# Revit family: FP_Revit_18_CID834RDTB4_Cooktop_90001222A
name_source: partatom
category: Specialty Equipment
revit_build: Autodesk Revit 2018 (Build: 20170223_1515(x64)
units: mm (PartAtom-declared; Revit-internal decimal feet)

## family parameters
Always vertical = Yes
Cut with Voids When Loaded = Yes
OmniClass Number = 23.40.40.14.17.11
OmniClass Title = Cookers, Ovens, Stoves
Part Type = Normal
Room Calculation Point = No
Round Connector Dimension = Use Diameter
Shared = No
Work Plane-Based = No

## types (3) — shared parameters
Cavity - Depth = 492 mm
Cavity - Width = 807 mm
Chassis - Depth = 490 mm
Chassis - Height = 52 mm
Chassis - Width = 800 mm
Clearance - Below Cooktop = 415 mm
Clearance - Overhead Non-Combustible = 500 mm  [stored 1.64042 ft]
Clearance - Rear = 50 mm  [stored 0.164042 ft]
Clearance - Side Combustible = 40 mm
Connector Description - Electrical = 220 - 240 V, or 380 - 415 V 2N or 380 - 415 V 3N, 34 A, 7400 W, 50 Hz
Description = 83cm Induction Cooktop with integrated ventilation
Manufacturer = Fisher & Paykel Appliances
Material - Body = Fisher & Paykel - Grey
Material - Cooktop = Fisher & Paykel - Glass, Black
Material - Trim = Fisher & Paykel - Aluminium, Dark
Model = CID834RDTB4
Product - Depth = 534 mm
Product - Height = 217 mm
Product - Width = 830 mm  [stored 2.7231 ft]
URL = www.fisherpaykel.com
Visibility - Clearance Required = Yes

## per-type parameters (varying)
| type | Visibility - Ducted through Toe Kick Panel | Visibility - Ducted to Rear | Visibility - Ducting |
| CID834RDTB4 - Ducted through Toe Kick Panel | Yes | No | Yes |
| CID834RDTB4 - Ducted to Rear | No | Yes | Yes |
| CID834RDTB4 - Without Ducting | No | No | No |

note: [stored X ft] marks values corroborated as IEEE doubles in the binary element streams (Revit-internal decimal feet)

## geometry (parser evidence)
native form markers: Sweep x11
no freeform markers — native parametric forms only
